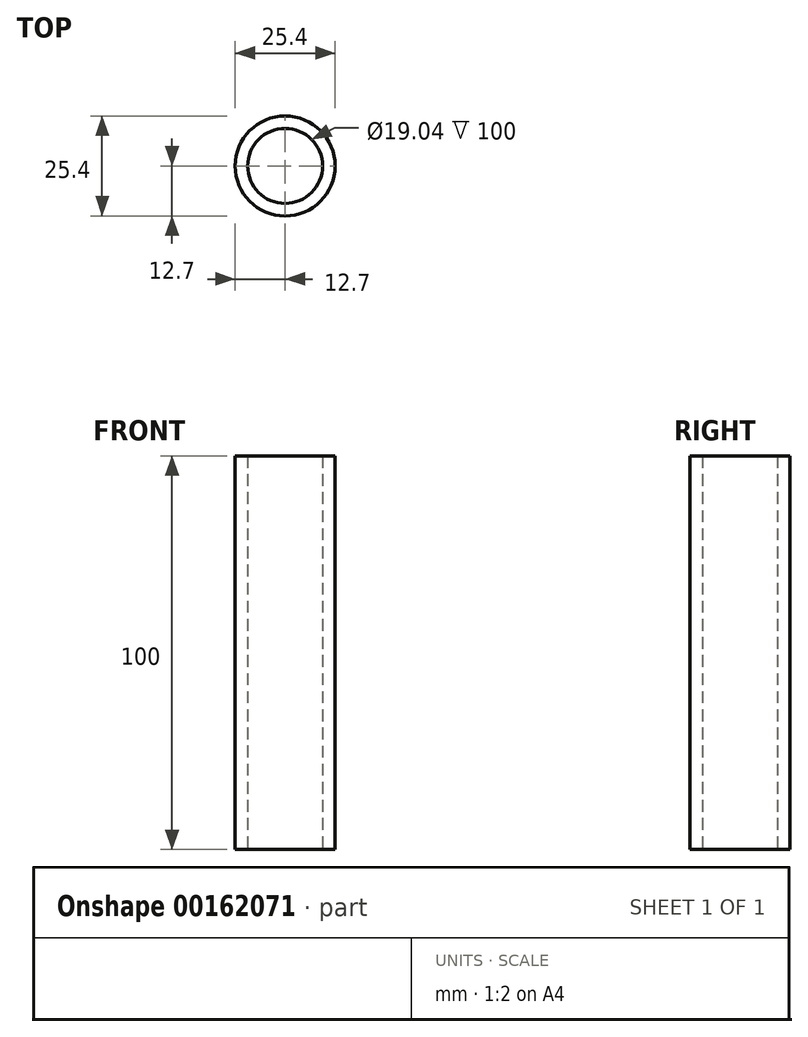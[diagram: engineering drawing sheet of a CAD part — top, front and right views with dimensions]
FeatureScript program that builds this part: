
annotation { "Feature Type Name" : "Feature", "Feature Type Description" : "" }
export const myFeature = defineFeature(function(context is Context, id is Id, definition is map)
    precondition{}
    {
        {
            var Q0;
            Q0=qCreatedBy(makeId("Top.planeOp"),FACE);
            var sketch = newSketch(context, id + "F0", { "sketchPlane" : qUnion([Q0])});
            skCircle(sketch, "E0", {"center": v(0, 0) * mm, "radius": 12.7 * mm});
            skCircle(sketch, "E1", {"center": v(0, 0) * mm, "radius": 9.52 * mm});
            skSolve(sketch);
        }
        {
            var Q0;
            Q0=makeQuery(id+"F0.imprint","IMPRINT",FACE,{"disambiguationData":[TD([[makeQuery(id+"F0.imprint","IMPRINT",EDGE,{"derivedFrom":sQuery(id+"F0.wireOp",EDGE,"E0")}),1.0]])]});
            extrude(context, id + "F1", {"entities" : qUnion([Q0]), "depth" : 100 * mm});
        }
    });
